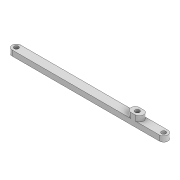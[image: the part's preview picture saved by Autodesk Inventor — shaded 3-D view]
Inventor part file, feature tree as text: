
AUTODESK INVENTOR PART (.ipt)
format: ipt  version: 2022 (Build 260153000, 153)  size: 113,664 bytes
history: native  units: mm
features: extrude x2, sketch x2, projected_geometry x1
ambient origin geometry x8: Origin, YZ Plane, XZ Plane, XY Plane, X Axis, Y Axis, Z Axis, Center Point
bodies: Solid1 (feature_tree)
feature tree (5):
  extrude  "Extrusion1"  Depth=8.0mm
  extrude  "Extrusion7"  Depth=5.0mm TaperAngle=0.0deg
  sketch  "Sketch1"  dims[d0=138.695mm d1=8.0mm]
  sketch  "Sketch4"  dims[d2=4.2mm d4=5.0mm d5=0.0mm d10=4.2mm d28=4.2mm d29=113.917mm d30=8.0mm d31=8.0mm d32=8.0mm d33=2.0mm d34=2.0mm d35=5.0mm d36=0.0mm]
  projected_geometry  "Projected Loop3"
